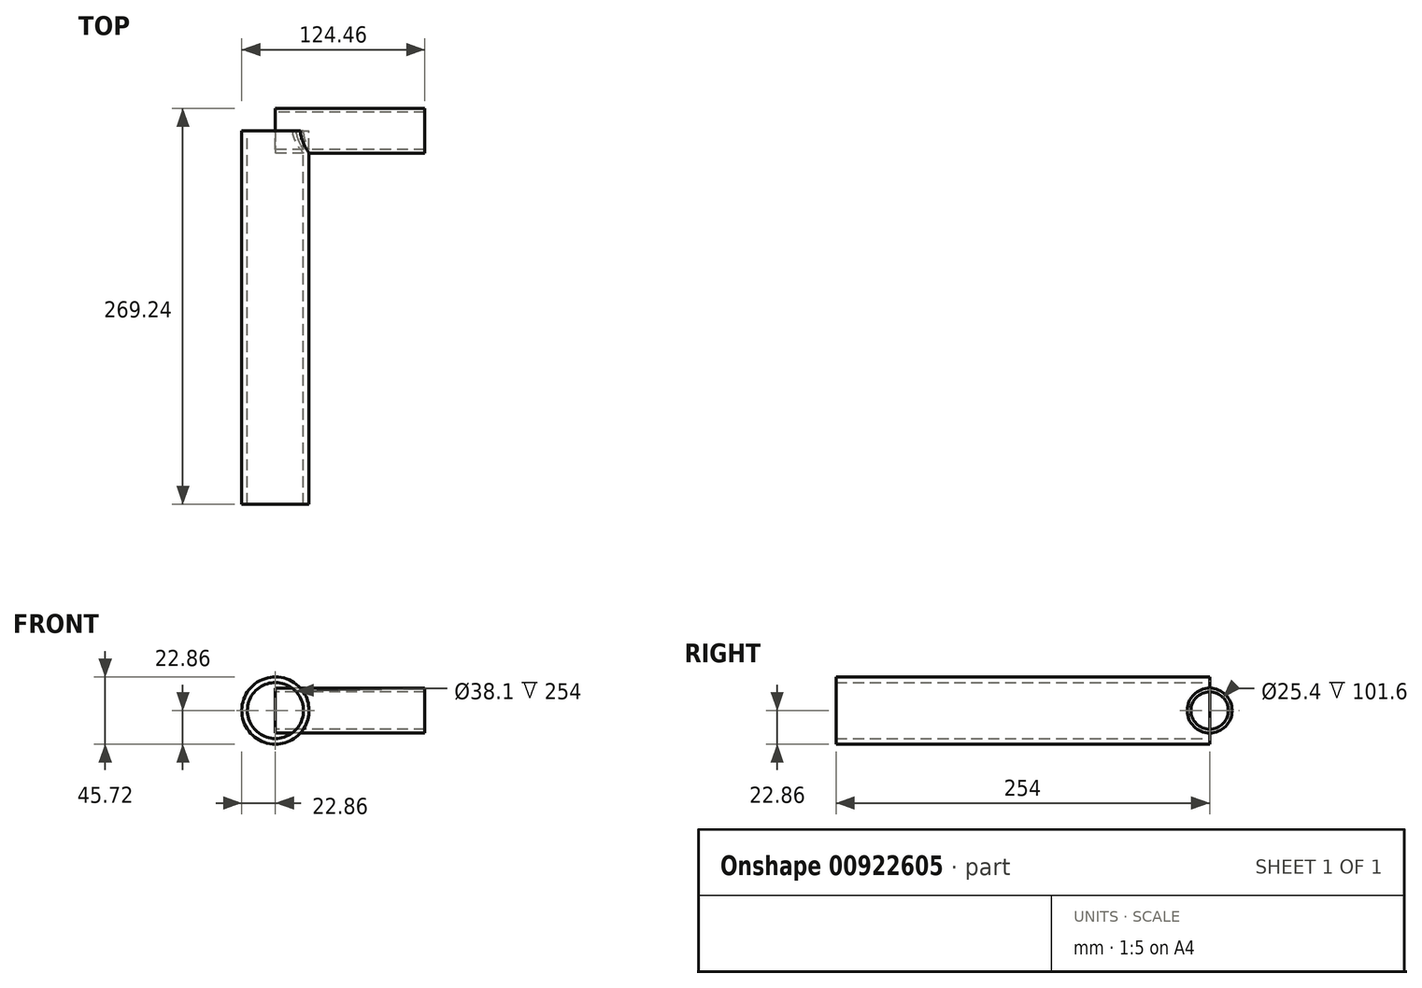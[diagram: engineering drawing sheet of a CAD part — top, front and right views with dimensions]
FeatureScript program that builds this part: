
annotation { "Feature Type Name" : "Feature", "Feature Type Description" : "" }
export const myFeature = defineFeature(function(context is Context, id is Id, definition is map)
    precondition{}
    {
        {
            var Q0;
            Q0=qCreatedBy(makeId("Front.planeOp"),FACE);
            var sketch = newSketch(context, id + "F0", { "sketchPlane" : qUnion([Q0])});
            skCircle(sketch, "E0", {"center": v(0, 0) * mm, "radius": 19.05 * mm});
            skCircle(sketch, "E1.0", {"center": v(0, 0) * mm, "radius": 22.86 * mm});
            skSolve(sketch);
        }
        {
            var Q0;
            Q0=makeQuery(id+"F0.imprint","IMPRINT",FACE,{"disambiguationData":[TD([[makeQuery(id+"F0.imprint","IMPRINT",EDGE,{"derivedFrom":sQuery(id+"F0.wireOp",EDGE,"E0")}),-1.0]])]});
            extrude(context, id + "F1", {"entities" : qUnion([Q0]), "depth" : 254 * mm, "offsetDistance" : 25.4 * mm});
        }
        {
            var Q0;
            Q0=qCreatedBy(makeId("Right.planeOp"),FACE);
            var sketch = newSketch(context, id + "F2", { "sketchPlane" : qUnion([Q0])});
            skCircle(sketch, "E2", {"center": v(0, 0) * mm, "radius": 12.7 * mm});
            skCircle(sketch, "E3.0", {"center": v(0, 0) * mm, "radius": 15.24 * mm});
            skSolve(sketch);
        }
        {
            var Q0;
            Q0=makeQuery(id+"F2.imprint","IMPRINT",FACE,{"disambiguationData":[TD([[makeQuery(id+"F2.imprint","IMPRINT",EDGE,{"derivedFrom":sQuery(id+"F2.wireOp",EDGE,"E2")}),-1.0]])]});
            extrude(context, id + "F3", {"entities" : qUnion([Q0]), "operationType" : NewBodyOperationType.ADD, "depth" : 101.6 * mm, "offsetDistance" : 25.4 * mm});
        }
    });
